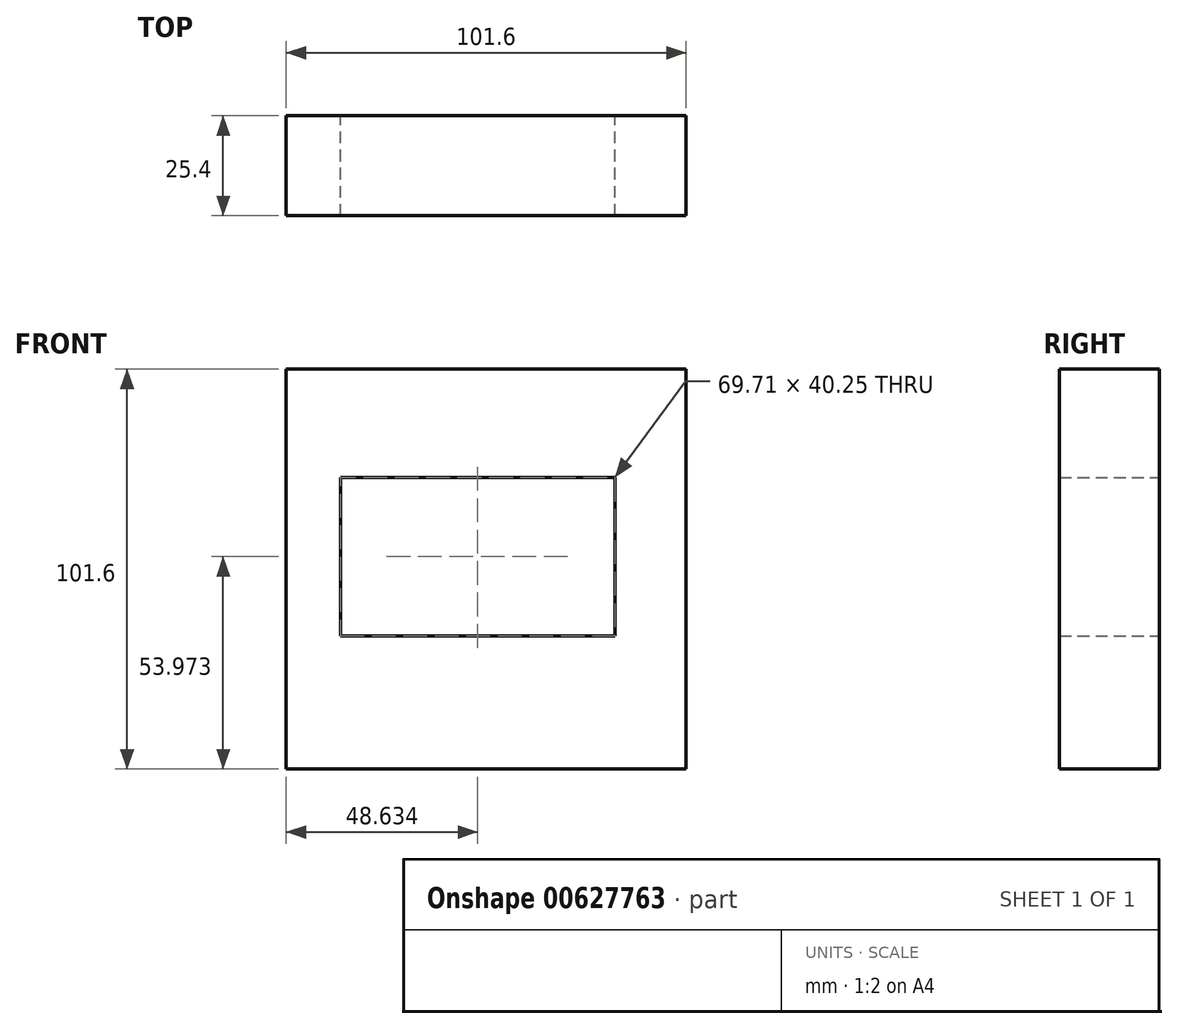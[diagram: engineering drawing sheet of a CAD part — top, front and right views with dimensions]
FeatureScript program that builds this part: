
annotation { "Feature Type Name" : "Feature", "Feature Type Description" : "" }
export const myFeature = defineFeature(function(context is Context, id is Id, definition is map)
    precondition{}
    {
        {
            var Q0;
            Q0=qCreatedBy(makeId("Front.planeOp"),FACE);
            var sketch = newSketch(context, id + "F0", { "sketchPlane" : qUnion([Q0])});
            skLineSegment(sketch, "E0", {"start": v(-66.89, 67.75) * mm, "end": v(-66.89, -33.85) * mm});
            skLineSegment(sketch, "E1", {"start": v(-66.89, -33.85) * mm, "end": v(34.71, -33.85) * mm});
            skLineSegment(sketch, "E2", {"start": v(34.71, -33.85) * mm, "end": v(34.71, 67.75) * mm});
            skLineSegment(sketch, "E3", {"start": v(34.71, 67.75) * mm, "end": v(-66.89, 67.75) * mm});
            skPoint(sketch, "E4.startSnap0", {"position": v(-16.09, 67.75) * mm});
            skLineSegment(sketch, "E5.bottom", {"start": v(16.6, 0) * mm, "end": v(-53.1, 0) * mm});
            skLineSegment(sketch, "E5.top", {"start": v(16.6, 40.25) * mm, "end": v(-53.1, 40.25) * mm});
            skLineSegment(sketch, "E5.left", {"start": v(16.6, 0) * mm, "end": v(16.6, 40.25) * mm});
            skLineSegment(sketch, "E5.right", {"start": v(-53.1, 0) * mm, "end": v(-53.1, 40.25) * mm});
            skPoint(sketch, "E5.middle", {"position": v(-18.26, 20.12) * mm});
            skPoint(sketch, "E4.end.orphan", {"position": v(-16.09, 67.75) * mm});
            skPoint(sketch, "E4.start.orphan", {"position": v(-16.09, 42.35) * mm});
            skSolve(sketch);
        }
        {
            var Q0;
            Q0=makeQuery(id+"F0.imprint","IMPRINT",FACE,{"disambiguationData":[TD([[makeQuery(id+"F0.imprint","IMPRINT",EDGE,{"derivedFrom":sQuery(id+"F0.wireOp",EDGE,"E0")}),1.0]])]});
            extrude(context, id + "F1", {"entities" : qUnion([Q0]), "depth" : 25.4 * mm, "offsetDistance" : 25.4 * mm});
        }
    });
